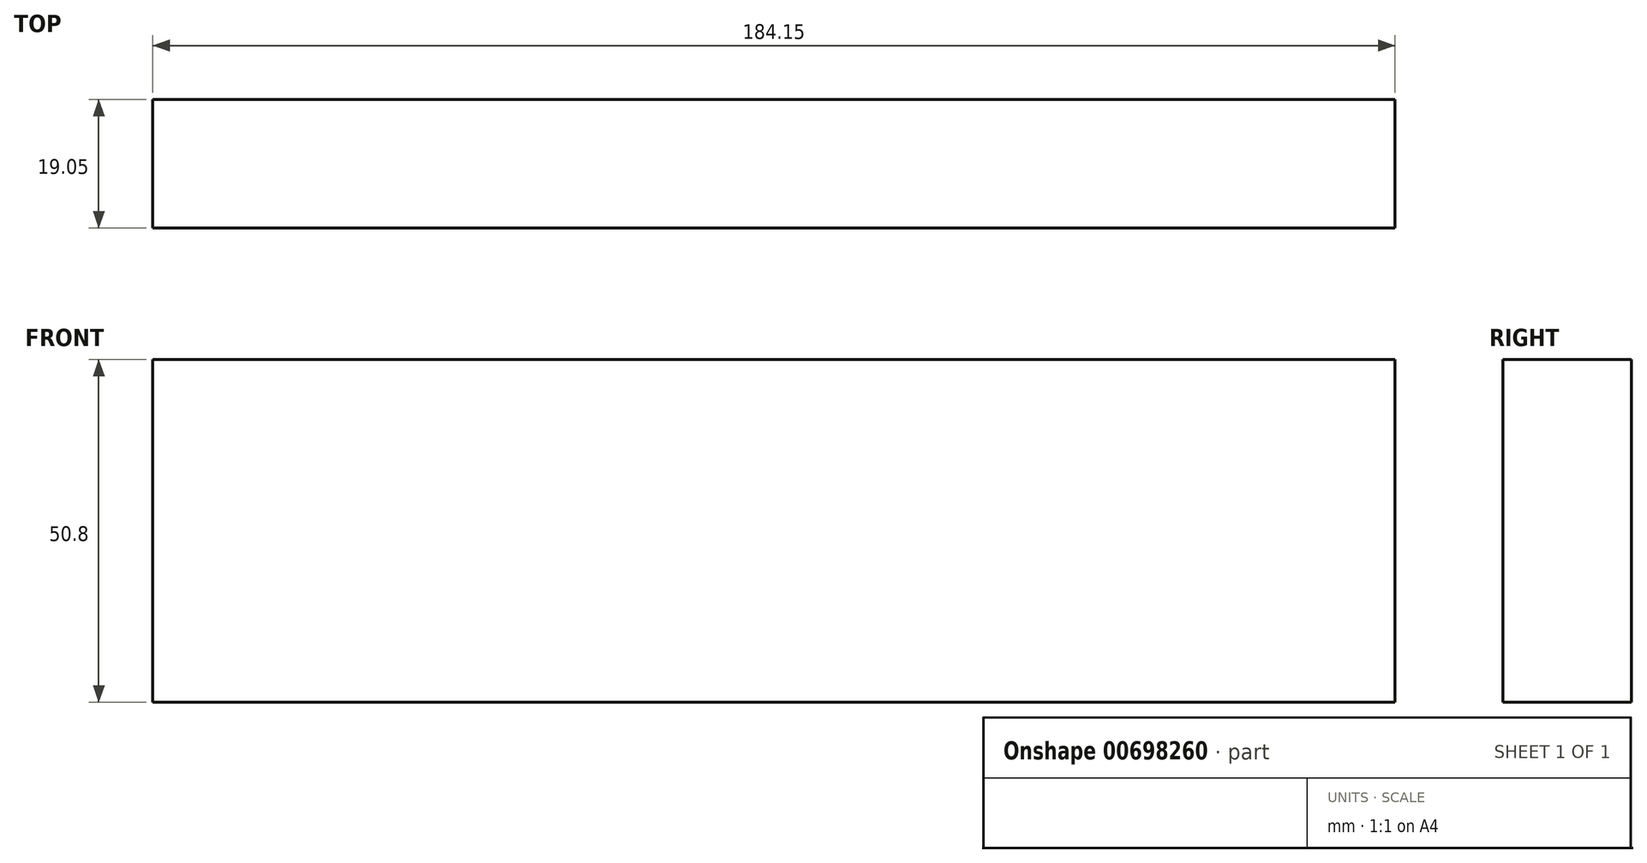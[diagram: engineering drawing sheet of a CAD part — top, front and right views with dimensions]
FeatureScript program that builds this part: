
annotation { "Feature Type Name" : "Feature", "Feature Type Description" : "" }
export const myFeature = defineFeature(function(context is Context, id is Id, definition is map)
    precondition{}
    {
        {
            var Q0;
            Q0=qCreatedBy(makeId("Front.planeOp"),FACE);
            var sketch = newSketch(context, id + "F0", { "sketchPlane" : qUnion([Q0])});
            skLineSegment(sketch, "E0.bottom", {"start": v(-103.62, 27.88) * mm, "end": v(80.53, 27.88) * mm});
            skLineSegment(sketch, "E0.top", {"start": v(-103.62, -22.92) * mm, "end": v(80.53, -22.92) * mm});
            skLineSegment(sketch, "E0.left", {"start": v(-103.62, 27.88) * mm, "end": v(-103.62, -22.92) * mm});
            skLineSegment(sketch, "E0.right", {"start": v(80.53, 27.88) * mm, "end": v(80.53, -22.92) * mm});
            skSolve(sketch);
        }
        {
            var Q0;
            Q0=makeQuery(id+"F0.imprint","IMPRINT",FACE,{"disambiguationData":[TD([[makeQuery(id+"F0.imprint","IMPRINT",EDGE,{"derivedFrom":sQuery(id+"F0.wireOp",EDGE,"E0.bottom")}),-1.0]])]});
            extrude(context, id + "F1", {"entities" : qUnion([Q0]), "depth" : 19.05 * mm, "offsetDistance" : 25.4 * mm});
        }
    });
